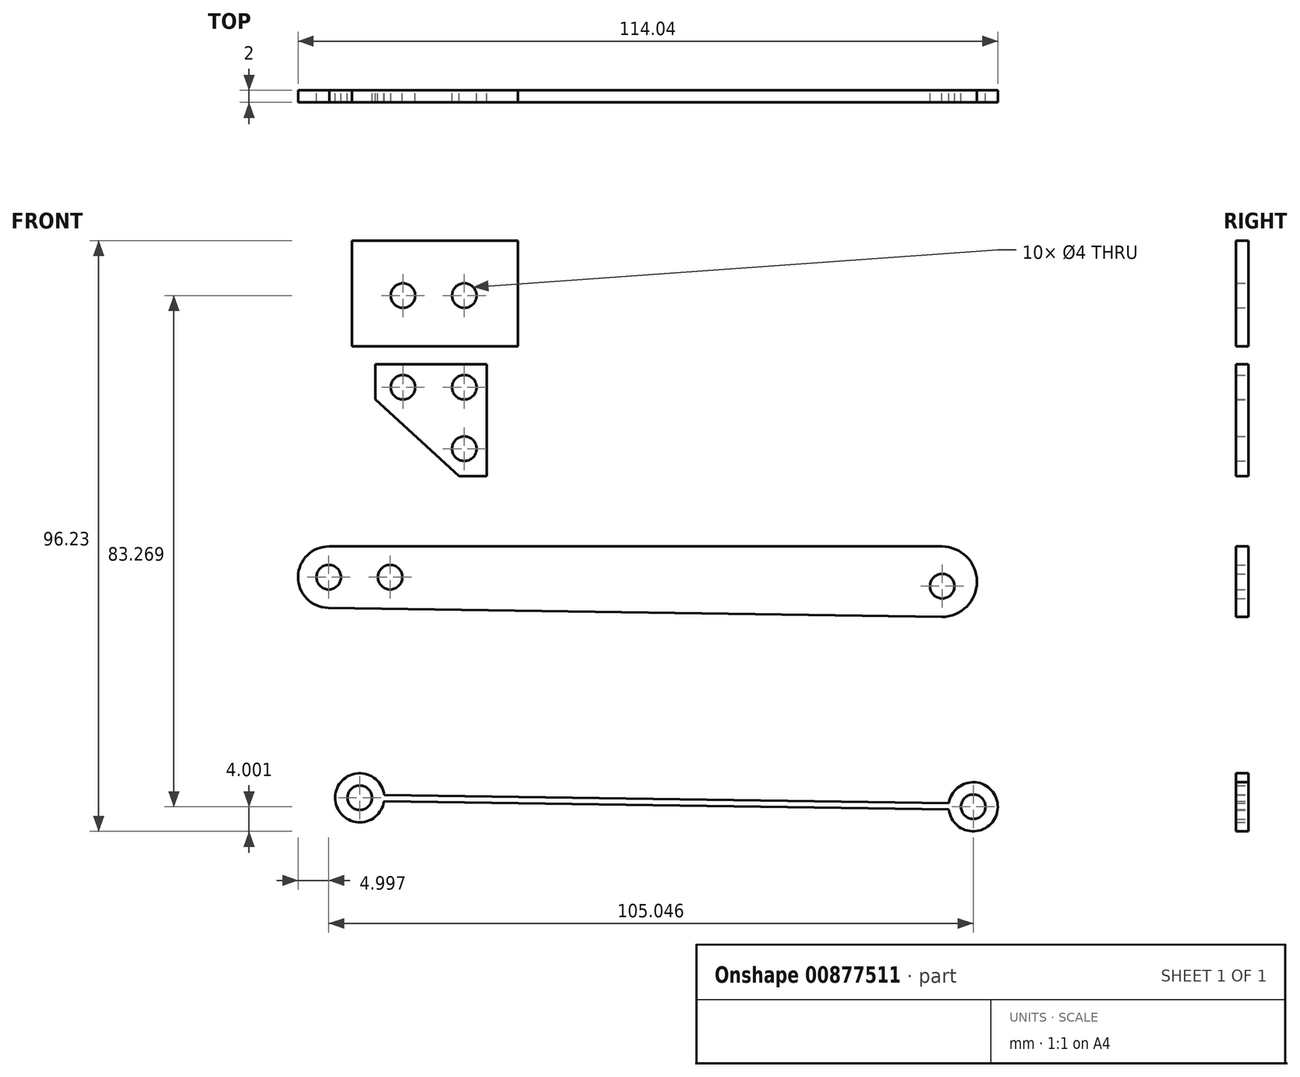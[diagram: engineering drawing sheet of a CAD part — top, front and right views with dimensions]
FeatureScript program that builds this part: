
annotation { "Feature Type Name" : "Feature", "Feature Type Description" : "" }
export const myFeature = defineFeature(function(context is Context, id is Id, definition is map)
    precondition{}
    {
        {
            var Q0;
            Q0=qCreatedBy(makeId("Front.planeOp"),FACE);
            var sketch = newSketch(context, id + "F0", { "sketchPlane" : qUnion([Q0])});
            skCircle(sketch, "E0", {"center": v(0, 0) * mm, "radius": 2 * mm});
            skCircle(sketch, "E1", {"center": v(10, 0) * mm, "radius": 2 * mm});
            skLineSegment(sketch, "E2.bottom", {"start": v(-8.35, 8.96) * mm, "end": v(18.75, 8.96) * mm});
            skLineSegment(sketch, "E2.top", {"start": v(-8.35, -8.28) * mm, "end": v(18.75, -8.28) * mm});
            skLineSegment(sketch, "E2.left", {"start": v(-8.35, 8.96) * mm, "end": v(-8.35, -8.28) * mm});
            skLineSegment(sketch, "E2.right", {"start": v(18.75, 8.96) * mm, "end": v(18.75, -8.28) * mm});
            skSolve(sketch);
        }
        {
            var Q0;
            Q0 = qSketchRegion(id + "F0", true);
            extrude(context, id + "F1", {"entities" : qUnion([Q0]), "depth" : 2 * mm, "offsetDistance" : 25 * mm});
        }
        {
            var Q0;
            Q0=qCreatedBy(makeId("Front.planeOp"),FACE);
            var sketch = newSketch(context, id + "F2", { "sketchPlane" : qUnion([Q0])});
            skCircle(sketch, "E3", {"center": v(0, -14.94) * mm, "radius": 2 * mm});
            skCircle(sketch, "E4", {"center": v(10, -14.94) * mm, "radius": 2 * mm});
            skCircle(sketch, "E5", {"center": v(10, -24.94) * mm, "radius": 2 * mm});
            skLineSegment(sketch, "E6", {"start": v(-4.54, -11.18) * mm, "end": v(13.65, -11.18) * mm});
            skLineSegment(sketch, "E7", {"start": v(13.65, -11.18) * mm, "end": v(13.65, -29.4) * mm});
            skLineSegment(sketch, "E8", {"start": v(13.65, -29.4) * mm, "end": v(9.17, -29.4) * mm});
            skLineSegment(sketch, "E9", {"start": v(9.17, -29.4) * mm, "end": v(-4.54, -16.9) * mm});
            skLineSegment(sketch, "E10", {"start": v(-4.54, -16.9) * mm, "end": v(-4.54, -11.18) * mm});
            skSolve(sketch);
        }
        {
            var Q0;
            Q0 = qSketchRegion(id + "F2", true);
            extrude(context, id + "F3", {"entities" : qUnion([Q0]), "depth" : 2 * mm, "offsetDistance" : 25 * mm});
        }
        {
            var Q0;
            Q0=qCreatedBy(makeId("Front.planeOp"),FACE);
            var sketch = newSketch(context, id + "F4", { "sketchPlane" : qUnion([Q0])});
            skCircle(sketch, "E11", {"center": v(-12.1, -45.87) * mm, "radius": 2 * mm});
            skCircle(sketch, "E12", {"center": v(87.89, -47.34) * mm, "radius": 2 * mm});
            skLineSegment(sketch, "E13.0", {"start": v(-12.03, -40.87) * mm, "end": v(87.81, -40.87) * mm});
            skLineSegment(sketch, "E14.0", {"start": v(-12.18, -50.87) * mm, "end": v(87.81, -52.34) * mm});
            skArc(sketch, "E15", {"start": v(87.81, -40.87) * mm, "mid": v(93.55, -46.6) * mm, "end": v(87.81, -52.34) * mm});
            skArc(sketch, "E16", {"start": v(-12.18, -50.87) * mm, "mid": v(-17.1, -45.8) * mm, "end": v(-12.03, -40.87) * mm});
            skCircle(sketch, "E17", {"center": v(-2.1, -45.87) * mm, "radius": 2 * mm});
            skSolve(sketch);
        }
        {
            var Q0;
            Q0 = qSketchRegion(id + "F4", true);
            extrude(context, id + "F5", {"entities" : qUnion([Q0]), "depth" : 2 * mm, "offsetDistance" : 25 * mm});
        }
        {
            var Q0;
            Q0=qCreatedBy(makeId("Front.planeOp"),FACE);
            var sketch = newSketch(context, id + "F6", { "sketchPlane" : qUnion([Q0])});
            skCircle(sketch, "E18", {"center": v(-7.05, -81.8) * mm, "radius": 2 * mm});
            skCircle(sketch, "E19", {"center": v(92.94, -83.27) * mm, "radius": 2 * mm});
            skLineSegment(sketch, "E20.0", {"start": v(88.98, -82.71) * mm, "end": v(-3.07, -81.36) * mm});
            skLineSegment(sketch, "E21.0", {"start": v(88.97, -83.71) * mm, "end": v(-3.09, -82.36) * mm});
            skArc(sketch, "E22.0", {"start": v(88.97, -83.71) * mm, "mid": v(96.94, -83.33) * mm, "end": v(88.98, -82.71) * mm});
            skArc(sketch, "E23.0", {"start": v(-3.07, -81.36) * mm, "mid": v(-11.05, -81.74) * mm, "end": v(-3.09, -82.36) * mm});
            skSolve(sketch);
        }
        {
            var Q0;
            Q0 = qSketchRegion(id + "F6", true);
            extrude(context, id + "F7", {"entities" : qUnion([Q0]), "depth" : 2 * mm, "offsetDistance" : 25 * mm});
        }
    });
